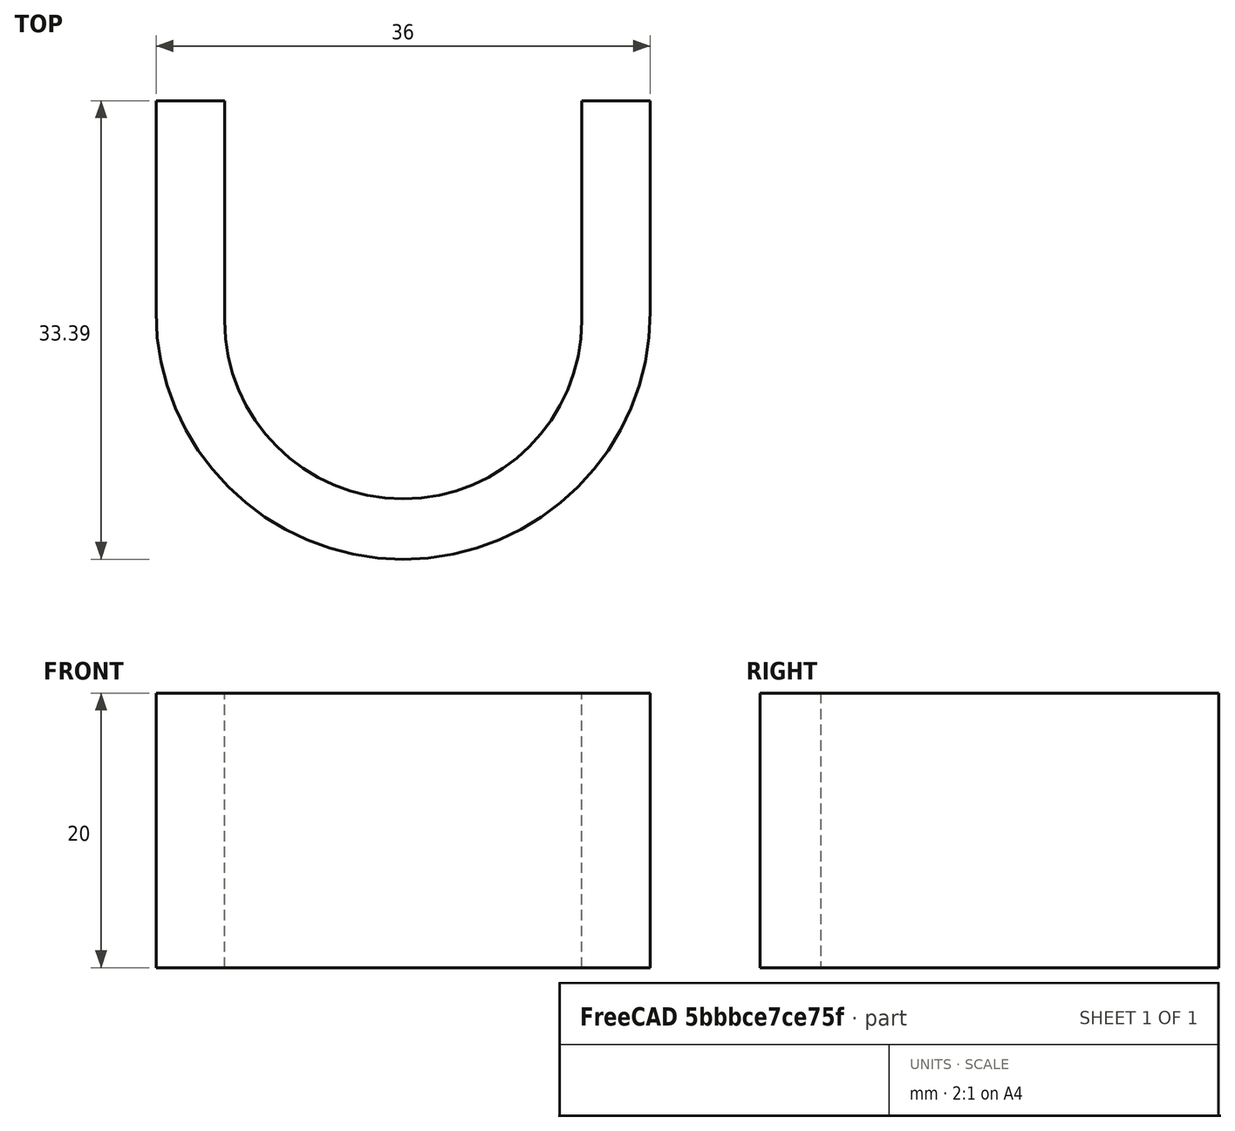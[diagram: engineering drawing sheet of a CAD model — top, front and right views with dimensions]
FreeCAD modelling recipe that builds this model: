
FCSTD DOCUMENT  (FreeCAD 0.16R)
Label: gimbal
License: All rights reserved
LicenseURL: http://en.wikipedia.org/wiki/All_rights_reserved
objects: Sketcher::SketchObject×2, PartDesign::Pad×1
note: 4 computed .brp shape members not serialized (recipe doc carries the construction recipe); baked Part::Feature solids carry a one-line shape summary decoded from their .brp

FEATURE [Sketcher::SketchObject] Sketch
  sketch-geometry (8):
    g0: ArcOfCircle CenterX=0 CenterY=17.3919 CenterZ=0 NormalX=0 NormalY=0 NormalZ=1 Radius=13 StartAngle=3.14159 EndAngle=6.28318
    g1: ArcOfCircle CenterX=0 CenterY=18.0001 CenterZ=0 NormalX=0 NormalY=0 NormalZ=1 Radius=18 StartAngle=3.1416 EndAngle=6.28318
    g2: LineSegment StartX=-18 StartY=18 StartZ=0 EndX=-18 EndY=33.3919 EndZ=0
    g3: LineSegment StartX=-13 StartY=17.3919 StartZ=0 EndX=-13 EndY=33.3919 EndZ=0
    g4: LineSegment StartX=13 StartY=17.3919 StartZ=0 EndX=13 EndY=33.3919 EndZ=0
    g5: LineSegment StartX=18 StartY=18 StartZ=0 EndX=18 EndY=33.3919 EndZ=0
    g6: LineSegment StartX=-18 StartY=33.3919 StartZ=0 EndX=-13 EndY=33.3919 EndZ=0
    g7: LineSegment StartX=13 StartY=33.3919 StartZ=0 EndX=18 EndY=33.3919 EndZ=0
  constraints (24):
    c: PointOnObject(g1,g-2)
    c: Symmetric(g0,g0,g-2)
    c: Symmetric(g1,g1,g-2)
    c: DistanceX(g1) = 18
    c: Coincident(g2,g1)
    c: Vertical(g2)
    c: Coincident(g3,g0)
    c: Vertical(g3)
    c: Coincident(g4,g0)
    c: Vertical(g4)
    c: Coincident(g5,g1)
    c: Vertical(g5)
    c: Horizontal(g6)
    c: Horizontal(g7)
    c: Coincident(g6,g2)
    c: Coincident(g7,g4)
    c: Coincident(g6,g3)
    c: Coincident(g7,g5)
    c: DistanceY(g3,g3) = 16
    c: DistanceY(g4,g4) = 16
    c: Radius(g1) = 18
    c: Radius(g0) = 13
    c: DistanceY(g-1,g1) = 18
    c: DistanceX(g0,g-1) = 13
FEATURE [PartDesign::Pad] Pad
  Length = 20
  Length2 = 100
  Sketch = -> Sketch
  Type = 0
FEATURE [Sketcher::SketchObject] Sketch001
  ExternalGeometry = -> [Pad]
  Placement = pos=(18,0,0) rot=(0.57735,0.57735,0.57735;2.0944rad)
  Support = -> Pad [Face7]
  sketch-geometry (5):
    g0: LineSegment StartX=30.0436 StartY=0 StartZ=0 EndX=30.0436 EndY=10 EndZ=0
    g1: LineSegment StartX=23.0436 StartY=9.23581 StartZ=0 EndX=23.0436 EndY=0 EndZ=0
    g2: ArcOfCircle CenterX=16.8029 CenterY=13.5453 CenterZ=0 NormalX=0 NormalY=0 NormalZ=1 Radius=3.5 StartAngle=1.22173 EndAngle=5.06145
    g3: ArcOfCircle CenterX=26.5436 CenterY=10 CenterZ=0 NormalX=0 NormalY=0 NormalZ=1 Radius=3.5 StartAngle=6.28319 EndAngle=7.50492
    g4: LineSegment StartX=18 StartY=16.8342 StartZ=0 EndX=27.7407 EndY=13.2889 EndZ=0
  constraints (20):
    c: Vertical(g0)
    c: Vertical(g1)
    c: PointOnObject(g1,g-1)
    c: PointOnObject(g0,g-1)
    c: DistanceX(g1,g0) = 7
    c: Radius(g2) = 3.5
    c: Radius(g3) = 3.5
    c: Coincident(g3,g0)
    c: Coincident(g3,g4)
    c: Coincident(g2,g4)
    c: Tangent(g4,g2)
    c: Tangent(g3,g4)
    c: Tangent(g0,g3)
    c: PointOnObject(g2,g-3)
    c: PointOnObject(g2,g-3)
    c: PointOnObject(g2,g-3)
    c: DistanceY(g0,g0) = 10
    c: Angle(g4) = -0.349066
    c: PointOnObject(g2,g-1)
    c: PointOnObject(g2,g-3)
